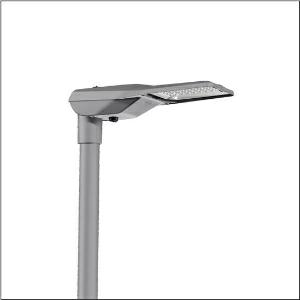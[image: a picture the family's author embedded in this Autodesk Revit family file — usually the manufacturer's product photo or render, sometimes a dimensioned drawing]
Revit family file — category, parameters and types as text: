
# Revit family: streetlight_sl_21_iq_mini___st1_0a_5xe2d21y08gb_b3c5
name_source: partatom
category: Lighting Fixtures
units: mm (PartAtom-declared; Revit-internal decimal feet)

## family parameters
Cut with Voids When Loaded = No
Host = Face
Light Source = No
Part Type = Normal
Room Calculation Point = No
Round Connector Dimension = Use Diameter
Shared = No

## types (1)
- --- (1 x LED, 4810 lm, 39.8 W, 2200K)
    Apparent Load = 40 VA
    CIE Flux Codes = 37 72 97 100 100
    Color Rendering = 70
    Color Temperature = 2200K
    Default Elevation = 1800 mm
    Description = Streetlight SL 21 iQ mini, mast luminaire, primary light control with lens, of PMMA, primary optical cover: cover, of toughened safety glass, transparent, light distribution: ST1.0a, light emission: direct distribution, primary light characteristic: asymmetric, installation type: post-top, side-entry, LED, High Power LED, rated luminous flux: 4.810lm, luminous efficacy: 121lm/W, light colour: 722, colour temperature: 2200K, control: presetting dimming logarithmic, Street-Remote, Auto-Match, Temp-Guard, Lumen-Switch, Night-Set, Smart-Wire, Light-Fading, Desk-Remote (wireless, voltage-free reading and setting of iQ features in the workshop via application-optimized NFC function/RFID function), optimised constant luminous flux control (CLO 2.0), mains connection: 220..240V, AC, 50/60Hz, start of lifetime: 40W, end of service life: 41W, reduction: 18W, luminaire housing, of diecast aluminium, powder-coated, Siteco® metallic grey (DB 702S), corrosivity category C5 mid according to DIN EN ISO 12944, please order mast flange separately, inclination adjustable: 0°, 5°, 10°, 15°, sealing non-destructively replaceable, multi-level sealing system, length: 628mm, width: 235mm, height: 110mm, mast flange for spigot size: 42mm (side-entry): 5XC10008XM4, 60/48mm (side-entry/post-top): 5XC10108XM2, 76/60mm (side-entry/post-top): 5XC10108XM1, Smart Interface below and above, protection rating (complete): IP66, insulation class (complete): insulation class II (safety insulation), certification: CE, ENEC, ENEC+, VDE, impact resistance: IK09, permissible operating ambient temperature for outdoor applications: -40..+50°C, standard-compliant lighting for roads and squares, packaging unit: 1 piece

Light Distribution: ST1.0a
    Height = 110 mm
    Lamp = 1 x LED
    Lamp Light Flux = 4810 lm
    Lamp Power = 39.8 W
    Lamp count = 1
    Length = 625 mm
    Luminous efficacy = 121 lm/W
    Manufacturer = Siteco
    ModVariant = No
    Model = 5XE2D21Y08GB
    Number of Poles = 1
    OnlyDefault = Yes
    Power Factor = 1
    Product Name = Streetlight SL 21 iQ mini | ST1.0a
    Product group = mast luminaire | pylon top
    ProductGroupID = 6100
    Protection Class = Protection class II
    Protection Degree = IP 66
    RLX_Detail_Level = 1
    RLX_Emergency_Light_Flux = 0 lm
    RLX_Emergency_Type = 0
    RLX_Emergency_Type_DB = No
    RlxData = <blob elided: 92597 chars, md5=dd901544>
    Socket = socket
    Standby Power = 0 W
    System Light Flux = 4810 lm
    System Power = 40 W
    Type Comments = factory setting: luminous flux: 100 % | dim-lin: 254 | 800 mA
    Type Image = l_1003514.jpg
    URL = http://relux.com
    VarID = @adj_045109
    Voltage = 0 V
    Weight = 0.00 kg
    Width = 234 mm

## geometry (parser evidence)
native form markers: Blend x4, Sweep x11
no freeform markers — native parametric forms only
